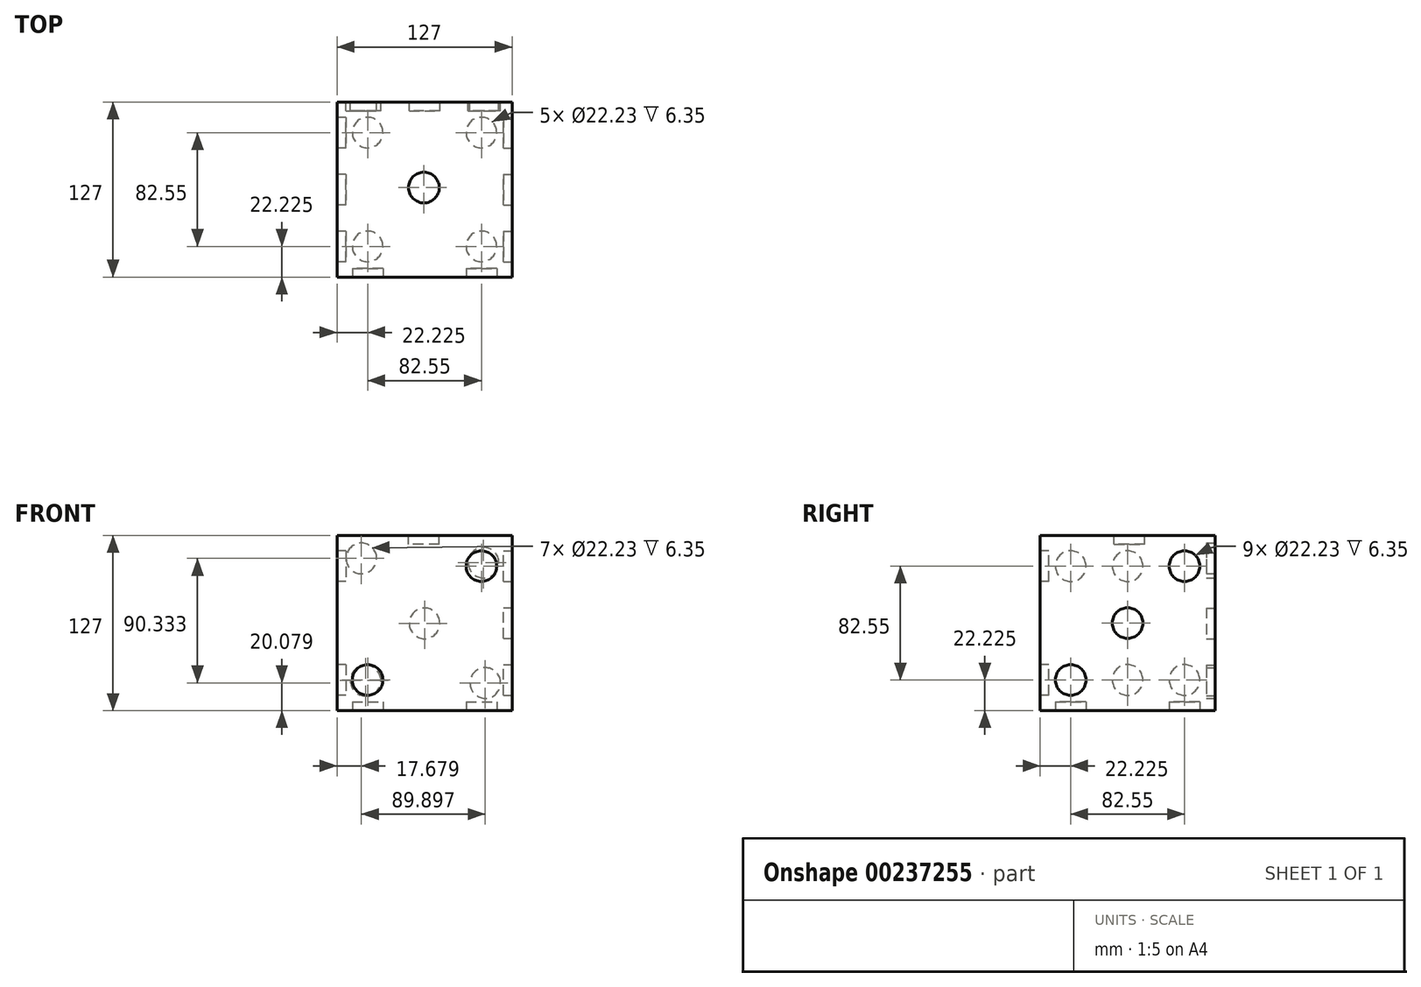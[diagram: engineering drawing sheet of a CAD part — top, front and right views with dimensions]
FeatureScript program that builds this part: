
annotation { "Feature Type Name" : "Feature", "Feature Type Description" : "" }
export const myFeature = defineFeature(function(context is Context, id is Id, definition is map)
    precondition{}
    {
        {
            var Q0;
            Q0=qCreatedBy(makeId("Top.planeOp"),FACE);
            var sketch = newSketch(context, id + "F0", { "sketchPlane" : qUnion([Q0])});
            skLineSegment(sketch, "E0.bottom", {"start": v(0, 0) * mm, "end": v(127, 0) * mm});
            skLineSegment(sketch, "E0.top", {"start": v(0, 127) * mm, "end": v(127, 127) * mm});
            skLineSegment(sketch, "E0.left", {"start": v(0, 0) * mm, "end": v(0, 127) * mm});
            skLineSegment(sketch, "E0.right", {"start": v(127, 0) * mm, "end": v(127, 127) * mm});
            skSolve(sketch);
        }
        {
            var Q0;
            Q0=makeQuery(id+"F0.imprint","IMPRINT",FACE,{"disambiguationData":[TD([[makeQuery(id+"F0.imprint","IMPRINT",EDGE,{"derivedFrom":sQuery(id+"F0.wireOp",EDGE,"E0.bottom")}),1.0]])]});
            extrude(context, id + "F1", {"entities" : qUnion([Q0]), "depth" : 127 * mm});
        }
        {
            var Q0;
            Q0=makeQuery(id+"F1.opExtrude","CAP_FACE",FACE,{"disambiguationData":[OSD([sQuery(id+"F0.wireOp",EDGE,"E0.bottom"),sQuery(id+"F0.wireOp",EDGE,"E0.top"),sQuery(id+"F0.wireOp",EDGE,"E0.left"),sQuery(id+"F0.wireOp",EDGE,"E0.right")])],"isStart":false});
            var sketch = newSketch(context, id + "F2", { "sketchPlane" : qUnion([Q0])});
            skCircle(sketch, "E1", {"center": v(63.05, 64.85) * mm, "radius": 11.11 * mm});
            skSolve(sketch);
        }
        {
            var Q0;
            Q0=makeQuery(id+"F2.imprint","IMPRINT",FACE,{"disambiguationData":[TD([[makeQuery(id+"F2.imprint","IMPRINT",EDGE,{"derivedFrom":sQuery(id+"F2.wireOp",EDGE,"E1")}),1.0]])]});
            var Q1;
            Q1=sQuery(id+"F2.wireOp",EDGE,"E1");
            extrude(context, id + "F3", {"entities" : qUnion([Q0]), "operationType" : NewBodyOperationType.REMOVE, "surfaceEntities" : qUnion([Q1]), "oppositeDirection" : true, "depth" : 6.35 * mm});
        }
        {
            var Q0;
            Q0=makeQuery(id+"F1.opExtrude","SWEPT_FACE",FACE,{"disambiguationData":[OSD([sQuery(id+"F0.wireOp",EDGE,"E0.bottom")])]});
            var sketch = newSketch(context, id + "F4", { "sketchPlane" : qUnion([Q0])});
            skSolve(sketch);
        }
        {
            var Q0;
            {var subQ0=sQuery(id+"F0.wireOp",EDGE,"E0.bottom");Q0=makeQuery(id+"F4.imprint","IMPRINT",FACE,{"disambiguationData":[TD([[makeQuery(id+"F4.imprint","IMPRINT",EDGE,{"derivedFrom":makeQuery(id+"F1.opExtrude","CAP_EDGE",EDGE,{"disambiguationData":[OSD([subQ0])],"isStart":true})}),1.0]])]});}
            var sketch = newSketch(context, id + "F5", { "sketchPlane" : qUnion([Q0])});
            skCircle(sketch, "E2", {"center": v(22.23, 22.22) * mm, "radius": 11.11 * mm});
            skCircle(sketch, "E3", {"center": v(104.78, 104.78) * mm, "radius": 11.11 * mm});
            skSolve(sketch);
        }
        {
            var Q0;
            Q0=makeQuery(id+"F1.opExtrude","SWEPT_FACE",FACE,{"disambiguationData":[OSD([sQuery(id+"F0.wireOp",EDGE,"E0.right")])]});
            var sketch = newSketch(context, id + "F6", { "sketchPlane" : qUnion([Q0])});
            skLineSegment(sketch, "E4", {"start": v(0, 0) * mm, "end": v(127, 127) * mm, "construction": true});
            skCircle(sketch, "E5", {"center": v(22.22, 22.23) * mm, "radius": 11.11 * mm});
            skCircle(sketch, "E6", {"center": v(63.5, 63.5) * mm, "radius": 11.11 * mm});
            skCircle(sketch, "E7", {"center": v(104.77, 104.78) * mm, "radius": 11.11 * mm});
            skSolve(sketch);
        }
        {
            var Q0;
            Q0 = qSketchRegion(id + "F6", true);
            extrude(context, id + "F7", {"entities" : qUnion([Q0]), "operationType" : NewBodyOperationType.REMOVE, "oppositeDirection" : true, "depth" : 6.35 * mm});
        }
        {
            var Q0;
            Q0 = qSketchRegion(id + "F5", true);
            extrude(context, id + "F8", {"entities" : qUnion([Q0]), "operationType" : NewBodyOperationType.REMOVE, "oppositeDirection" : true, "depth" : 6.35 * mm});
        }
        {
            var Q0;
            Q0=makeQuery(id+"F1.opExtrude","CAP_FACE",FACE,{"disambiguationData":[OSD([sQuery(id+"F0.wireOp",EDGE,"E0.bottom"),sQuery(id+"F0.wireOp",EDGE,"E0.top"),sQuery(id+"F0.wireOp",EDGE,"E0.left"),sQuery(id+"F0.wireOp",EDGE,"E0.right")])],"isStart":true});
            var sketch = newSketch(context, id + "F9", { "sketchPlane" : qUnion([Q0])});
            skLineSegment(sketch, "E8", {"start": v(104.78, -127) * mm, "end": v(104.78, 0) * mm, "construction": true});
            skLineSegment(sketch, "E9", {"start": v(22.23, -127) * mm, "end": v(22.22, 0) * mm, "construction": true});
            skSolve(sketch);
        }
        {
            var Q0;
            Q0=makeQuery(id+"F9.imprint","IMPRINT",FACE,{"disambiguationData":[TD([[makeQuery(id+"F9.imprint","IMPRINT",EDGE,{"derivedFrom":makeQuery(id+"F1.opExtrude","CAP_EDGE",EDGE,{"disambiguationData":[OSD([sQuery(id+"F0.wireOp",EDGE,"E0.bottom")])],"isStart":true})}),-1.0]])]});
            var sketch = newSketch(context, id + "F10", { "sketchPlane" : qUnion([Q0])});
            skCircle(sketch, "E10", {"center": v(104.77, -104.78) * mm, "radius": 11.11 * mm});
            skCircle(sketch, "E11", {"center": v(104.78, -22.23) * mm, "radius": 11.11 * mm});
            skCircle(sketch, "E12", {"center": v(22.23, -104.78) * mm, "radius": 11.11 * mm});
            skCircle(sketch, "E13", {"center": v(22.23, -22.22) * mm, "radius": 11.11 * mm});
            skSolve(sketch);
        }
        {
            var Q0;
            Q0 = qSketchRegion(id + "F10", true);
            extrude(context, id + "F11", {"entities" : qUnion([Q0]), "operationType" : NewBodyOperationType.REMOVE, "oppositeDirection" : true, "depth" : 6.35 * mm});
        }
        {
            var Q0;
            Q0=makeQuery(id+"F1.opExtrude","SWEPT_FACE",FACE,{"disambiguationData":[OSD([sQuery(id+"F0.wireOp",EDGE,"E0.top")])]});
            var sketch = newSketch(context, id + "F12", { "sketchPlane" : qUnion([Q0])});
            skLineSegment(sketch, "E14", {"start": v(0, 127) * mm, "end": v(-127, 0) * mm, "construction": true});
            skLineSegment(sketch, "E15", {"start": v(0, 0) * mm, "end": v(-127, 127) * mm, "construction": true});
            skSolve(sketch);
        }
        {
            var Q0;
            {var subQ0=sQuery(id+"F0.wireOp",EDGE,"E0.top");Q0=makeQuery(id+"F12.imprint","IMPRINT",FACE,{"disambiguationData":[TD([[makeQuery(id+"F12.imprint","IMPRINT",EDGE,{"derivedFrom":makeQuery(id+"F1.opExtrude","CAP_EDGE",EDGE,{"disambiguationData":[OSD([subQ0])],"isStart":true})}),-1.0]])]});}
            var sketch = newSketch(context, id + "F13", { "sketchPlane" : qUnion([Q0])});
            skCircle(sketch, "E16", {"center": v(-20.73, 21.82) * mm, "radius": 11.11 * mm});
            skCircle(sketch, "E17", {"center": v(-63.5, 63.28) * mm, "radius": 11.11 * mm});
            skCircle(sketch, "E18", {"center": v(-107.58, 20.08) * mm, "radius": 11.11 * mm});
            skCircle(sketch, "E19", {"center": v(-106.27, 107.36) * mm, "radius": 11.11 * mm});
            skCircle(sketch, "E20", {"center": v(-17.68, 110.41) * mm, "radius": 11.11 * mm});
            skSolve(sketch);
        }
        {
            var Q0;
            Q0 = qSketchRegion(id + "F13", true);
            extrude(context, id + "F14", {"entities" : qUnion([Q0]), "operationType" : NewBodyOperationType.REMOVE, "oppositeDirection" : true, "depth" : 6.35 * mm});
        }
        {
            var Q0;
            Q0=makeQuery(id+"F1.opExtrude","SWEPT_FACE",FACE,{"disambiguationData":[OSD([sQuery(id+"F0.wireOp",EDGE,"E0.left")])]});
            var sketch = newSketch(context, id + "F15", { "sketchPlane" : qUnion([Q0])});
            skLineSegment(sketch, "E21", {"start": v(0, 104.78) * mm, "end": v(-127, 104.77) * mm, "construction": true});
            skLineSegment(sketch, "E22", {"start": v(0, 22.23) * mm, "end": v(-127, 22.22) * mm, "construction": true});
            skCircle(sketch, "E23", {"center": v(-22.23, 104.78) * mm, "radius": 11.11 * mm});
            skCircle(sketch, "E24", {"center": v(-63.5, 104.77) * mm, "radius": 11.11 * mm});
            skCircle(sketch, "E25", {"center": v(-104.78, 104.78) * mm, "radius": 11.11 * mm});
            skCircle(sketch, "E26", {"center": v(-22.23, 22.23) * mm, "radius": 11.11 * mm});
            skCircle(sketch, "E27", {"center": v(-63.5, 22.23) * mm, "radius": 11.11 * mm});
            skCircle(sketch, "E28", {"center": v(-104.78, 22.22) * mm, "radius": 11.11 * mm});
            skSolve(sketch);
        }
        {
            var Q0;
            Q0 = qSketchRegion(id + "F15", true);
            extrude(context, id + "F16", {"entities" : qUnion([Q0]), "operationType" : NewBodyOperationType.REMOVE, "oppositeDirection" : true, "depth" : 6.35 * mm});
        }
    });
